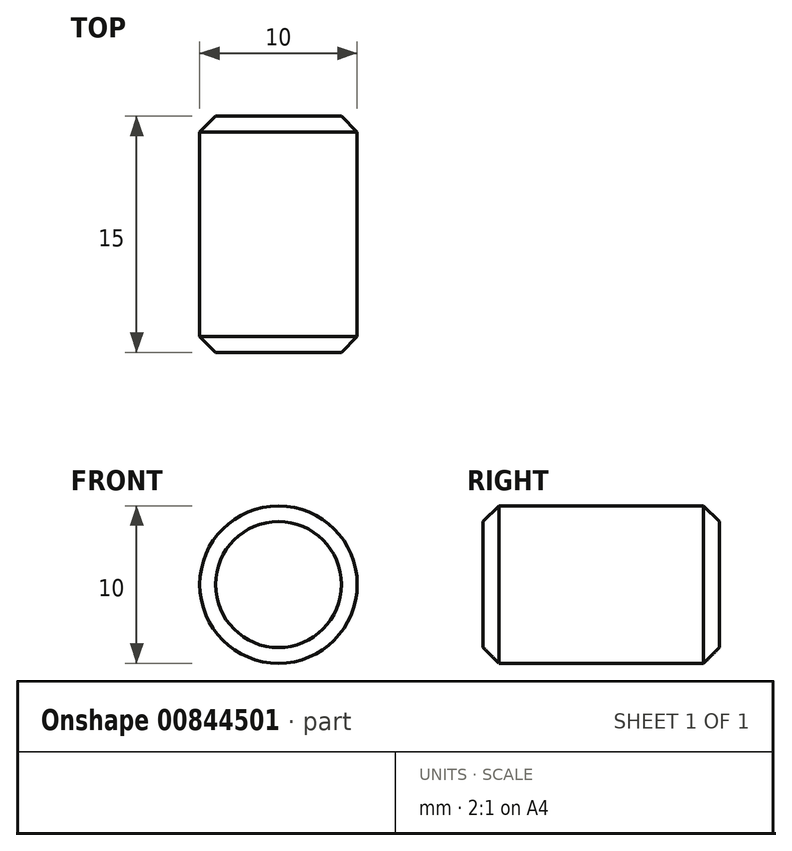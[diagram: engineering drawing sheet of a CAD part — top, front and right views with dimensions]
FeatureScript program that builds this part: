
annotation { "Feature Type Name" : "Feature", "Feature Type Description" : "" }
export const myFeature = defineFeature(function(context is Context, id is Id, definition is map)
    precondition{}
    {
        {
            var Q0;
            Q0=qCreatedBy(makeId("Front.planeOp"),FACE);
            var sketch = newSketch(context, id + "F0", { "sketchPlane" : qUnion([Q0])});
            skCircle(sketch, "E0", {"center": v(0, 0) * mm, "radius": 5 * mm});
            skSolve(sketch);
        }
        {
            var Q0;
            Q0=makeQuery(id+"F0.imprint","IMPRINT",FACE,{"disambiguationData":[TD([[makeQuery(id+"F0.imprint","IMPRINT",EDGE,{"derivedFrom":sQuery(id+"F0.wireOp",EDGE,"E0")}),1.0]])]});
            extrude(context, id + "F1", {"entities" : qUnion([Q0]), "depth" : 15 * mm, "offsetDistance" : 25 * mm});
        }
        {
            var Q0;
            Q0=makeQuery(id+"F1.opExtrude","CAP_EDGE",EDGE,{"disambiguationData":[OSD([sQuery(id+"F0.wireOp",EDGE,"E0")])],"isStart":true});
            chamfer(context, id + "F2", {"entities" : qUnion([Q0]), "width" : 1 * mm, "tangentPropagation" : true});
        }
        {
            var Q0;
            Q0=makeQuery(id+"F1.opExtrude","CAP_EDGE",EDGE,{"disambiguationData":[OSD([sQuery(id+"F0.wireOp",EDGE,"E0")])],"isStart":false});
            chamfer(context, id + "F3", {"entities" : qUnion([Q0]), "width" : 1 * mm, "tangentPropagation" : true});
        }
    });
